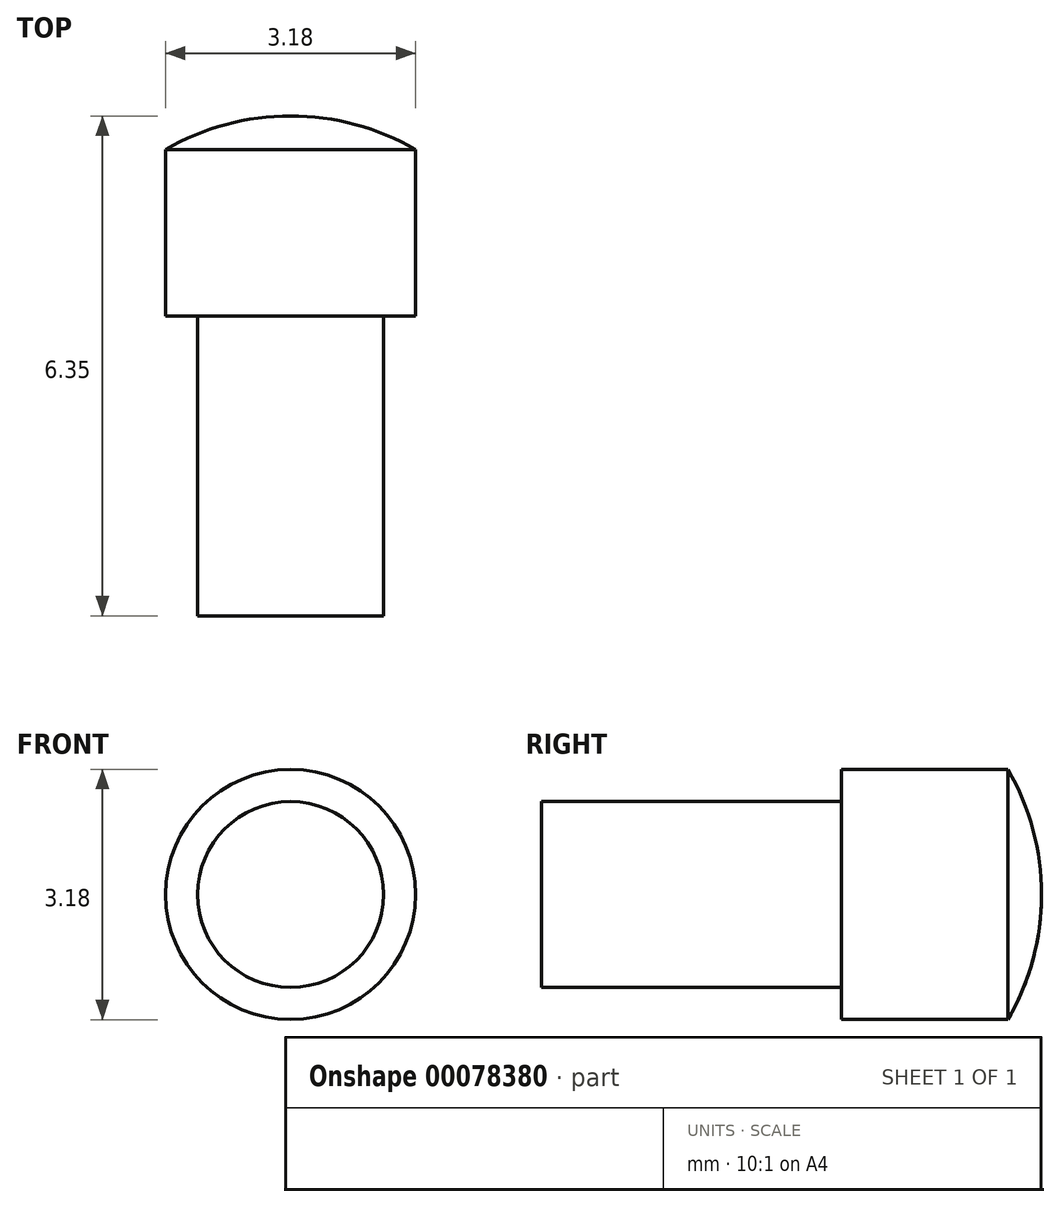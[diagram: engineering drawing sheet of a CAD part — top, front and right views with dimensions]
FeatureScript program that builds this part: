
annotation { "Feature Type Name" : "Feature", "Feature Type Description" : "" }
export const myFeature = defineFeature(function(context is Context, id is Id, definition is map)
    precondition{}
    {
        {
            var Q0;
            Q0=qCreatedBy(makeId("Right.planeOp"),FACE);
            var sketch = newSketch(context, id + "F0", { "sketchPlane" : qUnion([Q0])});
            skLineSegment(sketch, "E0", {"start": v(0, 0) * mm, "end": v(0, 1.18) * mm});
            skLineSegment(sketch, "E1", {"start": v(0, 1.18) * mm, "end": v(3.81, 1.18) * mm});
            skArc(sketch, "E2", {"start": v(6.35, 0) * mm, "mid": v(6.24, 0.82) * mm, "end": v(5.92, 1.59) * mm});
            skLineSegment(sketch, "E3", {"start": v(3.81, 1.59) * mm, "end": v(5.92, 1.59) * mm});
            skLineSegment(sketch, "E4", {"start": v(3.81, 1.59) * mm, "end": v(3.81, 1.18) * mm});
            skLineSegment(sketch, "E5", {"start": v(0, 0) * mm, "end": v(6.35, 0) * mm});
            skSolve(sketch);
        }
        {
            var Q0;
            Q0 = qSketchRegion(id + "F0", true);
            var Q1;
            Q1=sQuery(id+"F0.wireOp",EDGE,"E5");
            revolve(context, id + "F1", {"entities" : qUnion([Q0]), "axis" : qUnion([Q1]), "revolveType" : RevolveType.FULL});
        }
    });
